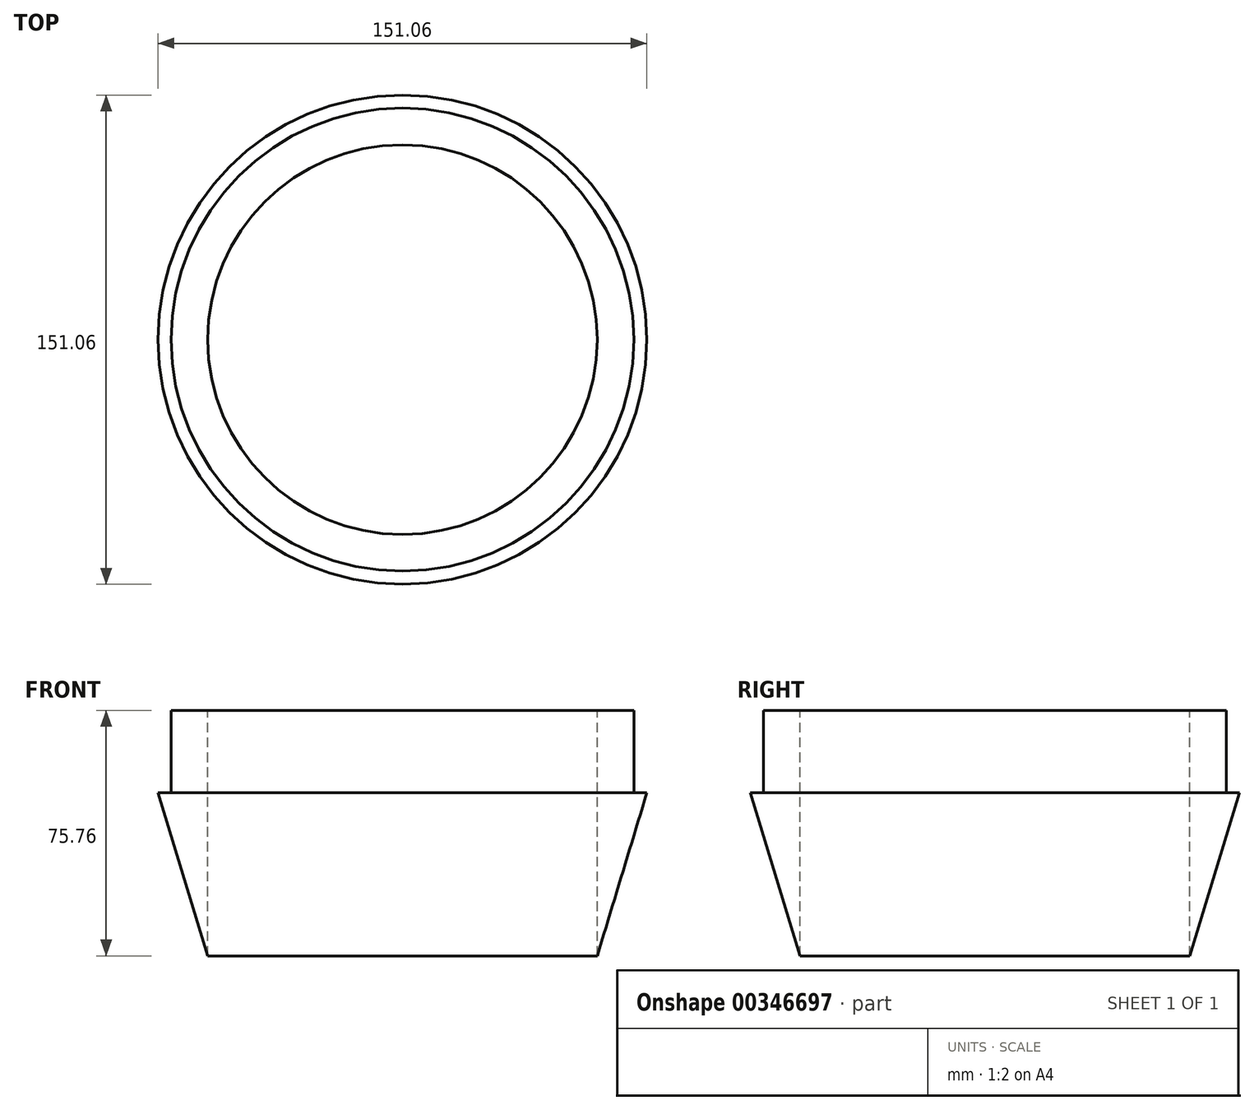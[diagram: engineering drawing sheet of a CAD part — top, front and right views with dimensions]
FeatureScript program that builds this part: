
annotation { "Feature Type Name" : "Feature", "Feature Type Description" : "" }
export const myFeature = defineFeature(function(context is Context, id is Id, definition is map)
    precondition{}
    {
        {
            var Q0;
            Q0=qCreatedBy(makeId("Front.planeOp"),FACE);
            var sketch = newSketch(context, id + "F0", { "sketchPlane" : qUnion([Q0])});
            skLineSegment(sketch, "E0", {"start": v(0, 0) * mm, "end": v(-60.17, 0) * mm});
            skLineSegment(sketch, "E1", {"start": v(-60.17, 0) * mm, "end": v(-75.53, 0) * mm});
            skLineSegment(sketch, "E2", {"start": v(-60.17, 0) * mm, "end": v(-60.17, -50.36) * mm});
            skLineSegment(sketch, "E3", {"start": v(-75.53, 0) * mm, "end": v(-60.17, -50.36) * mm});
            skLineSegment(sketch, "E4", {"start": v(0, 0) * mm, "end": v(0, -44.7) * mm});
            skSolve(sketch);
        }
        {
            var Q0;
            Q0 = qSketchRegion(id + "F0", true);
            var Q1;
            Q1=sQuery(id+"F0.wireOp",EDGE,"E4");
            revolve(context, id + "F1", {"entities" : qUnion([Q0]), "axis" : qUnion([Q1]), "revolveType" : RevolveType.FULL});
        }
        {
            var Q0;
            Q0=makeQuery(id+"F1.opRevolve","SWEPT_FACE",FACE,{"disambiguationData":[OSD([sQuery(id+"F0.wireOp",EDGE,"E1")])]});
            var sketch = newSketch(context, id + "F2", { "sketchPlane" : qUnion([Q0])});
            skCircle(sketch, "E5", {"center": v(0, 0) * mm, "radius": 71.47 * mm});
            skCircle(sketch, "E6", {"center": v(0, 0) * mm, "radius": 60.17 * mm});
            skSolve(sketch);
        }
        {
            var Q0;
            Q0 = qSketchRegion(id + "F2", true);
            extrude(context, id + "F3", {"entities" : qUnion([Q0]), "operationType" : NewBodyOperationType.ADD, "depth" : 25.4 * mm});
        }
    });
